# Revit family: Lighting-Wall_Mount-Lutron_Ivalo-Aliante_60
name_source: partatom
category: Lighting Fixtures
revit_build: Autodesk Revit 2015 (Build: 20140905_0730(x64)
units: mm (PartAtom-declared; Revit-internal decimal feet)

## types (4) — shared parameters
120 Volts = Yes
277 Volts = No
ADA Compliant = Yes
Assembly Code = D5020200
Brand = Ivalo Lighting
Color Filter = 16777215
Default Elevation = 6' - 0"
Dimming Lamp Color Temperature Shift = <None>
Fixture Shell Material = Aluminum - Lutron Ivalo - Anodized Clear
Lamp Quantity = 1
Load Classification = Lighting
Manufacturer = Lutron Electronics
Mounting = Wall Mounted
Number of Poles = 1
Overall Depth = 0' - 4"
Overall Height = 5' - 1 7/8"
Overall Width = 0' - 6 3/4"
Photometric Web File = Aliante 5ft Interior Sconce IES Data.ies
Product Page URL = http://www.ivalolighting.com
Product data url = https://bimobject.com
Series = Aliante
Tilt Angle = 0.00°
URL = http://www.lutron.com
Unit Weight = 12.50 lb
Version = 2
Voltage = 120 V

## per-type parameters (varying)
| type | Apparent Load | Description | Direct and Indirect Distribution | Indirect Distribution | Lamp | Lumens Per Lamp | Model | Slot Void Front Offset | Total Lumens | Wattage Comments |
| 80W T5 HO Direct and Indirect | 81 VA | Single Lamp Direct/Indirect Fluorescent Decorative Sconce | Yes | No | 80W T5 HO | 6160 lm | AND601802 | 0' - 3 1/8" | 6160 lm | 80.7W |
| 80W T5 HO Indirect | 81 VA | Single Lamp Indirect Fluorescent Decorative Sconce | No | Yes | 80W T5 HO | 6160 lm | ANN601802 | 0' - 6 1/4" | 6160 lm | 80.7W |
| 35W T5 HE Indirect | 35 VA | Single Lamp Indirect Fluorescent Decorative Sconce | No | Yes | 35W T5 HE | 3650 lm | ANN601352 | 0' - 6 1/4" | 3650 lm | 35W |
| 35W T5 HE Direct and Indirect | 35 VA | Single Lamp Direct/Indirect Fluorescent Decorative Sconce | Yes | No | 35W T5 HE | 3650 lm | AND601352 | 0' - 3 1/8" | 3650 lm | 35W |

## geometry (parser evidence)
native form markers: Sweep x3
no freeform markers — native parametric forms only
